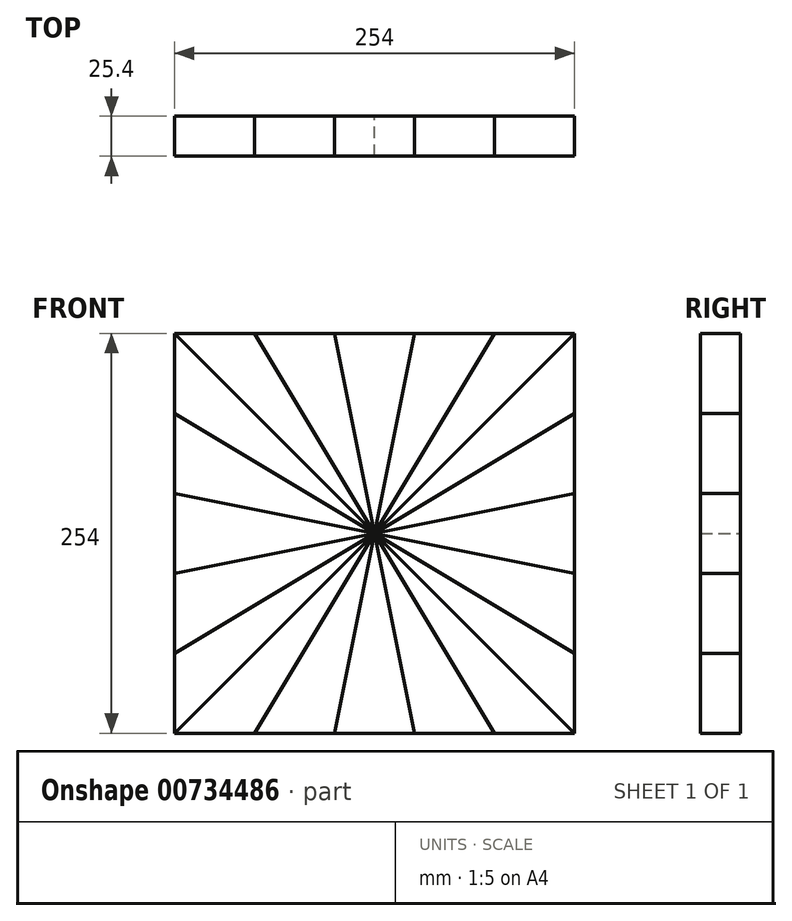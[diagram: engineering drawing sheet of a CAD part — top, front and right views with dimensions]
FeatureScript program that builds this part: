
annotation { "Feature Type Name" : "Feature", "Feature Type Description" : "" }
export const myFeature = defineFeature(function(context is Context, id is Id, definition is map)
    precondition{}
    {
        {
            var Q0;
            Q0=qCreatedBy(makeId("Front.planeOp"),FACE);
            var sketch = newSketch(context, id + "F0", { "sketchPlane" : qUnion([Q0])});
            skLineSegment(sketch, "E0.top", {"start": v(0, 127) * mm, "end": v(-127, 127) * mm});
            skLineSegment(sketch, "E1", {"start": v(0, 0) * mm, "end": v(-25.4, 127) * mm});
            skLineSegment(sketch, "E2", {"start": v(0, 0) * mm, "end": v(-127, 127) * mm});
            skPoint(sketch, "E3.end.orphan", {"position": v(-63.5, 127) * mm});
            skLineSegment(sketch, "E4", {"start": v(0, 0) * mm, "end": v(-76.2, 127) * mm});
            skLineSegment(sketch, "E5.MirrorCS", {"start": v(-127, 0) * mm, "end": v(-127, 127) * mm});
            skPoint(sketch, "E6.MirrorP", {"position": v(-127, 63.5) * mm});
            skLineSegment(sketch, "E7.MirrorCS", {"start": v(0, 0) * mm, "end": v(-127, 76.2) * mm});
            skLineSegment(sketch, "E8.MirrorCS", {"start": v(0, 0) * mm, "end": v(-127, 25.4) * mm});
            skLineSegment(sketch, "E9.MirrorCS", {"start": v(0, 0) * mm, "end": v(127, 25.4) * mm});
            skLineSegment(sketch, "E10.MirrorCS", {"start": v(0, 0) * mm, "end": v(127, 76.2) * mm});
            skPoint(sketch, "E11.MirrorP", {"position": v(63.5, 127) * mm});
            skPoint(sketch, "E12.MirrorP", {"position": v(127, 63.5) * mm});
            skLineSegment(sketch, "E13.MirrorCS", {"start": v(0, 0) * mm, "end": v(25.4, 127) * mm});
            skLineSegment(sketch, "E14.MirrorCS", {"start": v(0, 127) * mm, "end": v(127, 127) * mm});
            skLineSegment(sketch, "E15.MirrorCS", {"start": v(0, 0) * mm, "end": v(127, 127) * mm});
            skLineSegment(sketch, "E16.MirrorCS", {"start": v(127, 0) * mm, "end": v(127, 127) * mm});
            skLineSegment(sketch, "E17.MirrorCS", {"start": v(0, 0) * mm, "end": v(76.2, 127) * mm});
            skLineSegment(sketch, "E18.MirrorCS", {"start": v(0, -127) * mm, "end": v(127, -127) * mm});
            skLineSegment(sketch, "E19.MirrorCS", {"start": v(127, 0) * mm, "end": v(127, -127) * mm});
            skLineSegment(sketch, "E20.MirrorCS", {"start": v(0, 0) * mm, "end": v(-76.2, -127) * mm});
            skLineSegment(sketch, "E21.MirrorCS", {"start": v(0, 0) * mm, "end": v(-127, -25.4) * mm});
            skLineSegment(sketch, "E22.MirrorCS", {"start": v(0, 0) * mm, "end": v(76.2, -127) * mm});
            skPoint(sketch, "E23.MirrorP", {"position": v(127, -63.5) * mm});
            skLineSegment(sketch, "E24.MirrorCS", {"start": v(0, 0) * mm, "end": v(127, -25.4) * mm});
            skLineSegment(sketch, "E25.MirrorCS", {"start": v(0, 0) * mm, "end": v(-25.4, -127) * mm});
            skLineSegment(sketch, "E26.MirrorCS", {"start": v(0, 0) * mm, "end": v(127, -76.2) * mm});
            skLineSegment(sketch, "E27.MirrorCS", {"start": v(-127, 0) * mm, "end": v(-127, -127) * mm});
            skLineSegment(sketch, "E28.MirrorCS", {"start": v(0, 0) * mm, "end": v(25.4, -127) * mm});
            skPoint(sketch, "E29.MirrorP", {"position": v(63.5, -127) * mm});
            skLineSegment(sketch, "E30.MirrorCS", {"start": v(0, 0) * mm, "end": v(127, -127) * mm});
            skPoint(sketch, "E31.MirrorP", {"position": v(-63.5, -127) * mm});
            skLineSegment(sketch, "E32.MirrorCS", {"start": v(0, 0) * mm, "end": v(-127, -76.2) * mm});
            skPoint(sketch, "E33.MirrorP", {"position": v(-127, -63.5) * mm});
            skLineSegment(sketch, "E34.MirrorCS", {"start": v(0, 0) * mm, "end": v(-127, -127) * mm});
            skLineSegment(sketch, "E35.MirrorCS", {"start": v(0, -127) * mm, "end": v(-127, -127) * mm});
            skSolve(sketch);
        }
        {
            var Q0;
            {var subQ0=sQuery(id+"F0.wireOp",EDGE,"E2");Q0=makeQuery(id+"F0.imprint","IMPRINT",FACE,{"disambiguationData":[TD([[makeQuery(id+"F0.imprint","IMPRINT",EDGE,{"derivedFrom":subQ0}),1.0]])]});}
            extrude(context, id + "F1", {"entities" : qUnion([Q0]), "depth" : 25.4 * mm, "offsetDistance" : 25.4 * mm});
        }
        {
            var Q0;
            {var subQ0=sQuery(id+"F0.wireOp",EDGE,"E2");Q0=makeQuery(id+"F0.imprint","IMPRINT",FACE,{"disambiguationData":[TD([[makeQuery(id+"F0.imprint","IMPRINT",EDGE,{"derivedFrom":subQ0}),-1.0]])]});}
            extrude(context, id + "F2", {"entities" : qUnion([Q0]), "depth" : 25.4 * mm, "offsetDistance" : 25.4 * mm});
        }
        {
            var Q0;
            {var subQ0=sQuery(id+"F0.wireOp",EDGE,"E1");Q0=makeQuery(id+"F0.imprint","IMPRINT",FACE,{"disambiguationData":[TD([[makeQuery(id+"F0.imprint","IMPRINT",EDGE,{"derivedFrom":subQ0}),1.0]])]});}
            var Q1;
            {var subQ4=sQuery(id+"F0.wireOp",EDGE,"E25.MirrorCS");Q1=makeQuery(id+"F0.imprint","IMPRINT",FACE,{"disambiguationData":[TD([[makeQuery(id+"F0.imprint","IMPRINT",EDGE,{"derivedFrom":subQ4}),1.0]])]});}
            extrude(context, id + "F3", {"entities" : qUnion([Q0, Q1]), "depth" : 25.4 * mm, "offsetDistance" : 25.4 * mm});
        }
        {
            var Q0;
            {var subQ3=sQuery(id+"F0.wireOp",EDGE,"E1");Q0=makeQuery(id+"F0.imprint","IMPRINT",FACE,{"disambiguationData":[TD([[makeQuery(id+"F0.imprint","IMPRINT",EDGE,{"derivedFrom":subQ3}),-1.0]])]});}
            var Q1;
            {var subQ0=sQuery(id+"F0.wireOp",EDGE,"E20.MirrorCS");Q1=makeQuery(id+"F0.imprint","IMPRINT",FACE,{"disambiguationData":[TD([[makeQuery(id+"F0.imprint","IMPRINT",EDGE,{"derivedFrom":subQ0}),1.0]])]});}
            extrude(context, id + "F4", {"entities" : qUnion([Q0, Q1]), "depth" : 25.4 * mm, "offsetDistance" : 25.4 * mm});
        }
        {
            var Q0;
            {var subQ0=sQuery(id+"F0.wireOp",EDGE,"E13.MirrorCS");Q0=makeQuery(id+"F0.imprint","IMPRINT",FACE,{"disambiguationData":[TD([[makeQuery(id+"F0.imprint","IMPRINT",EDGE,{"derivedFrom":subQ0}),-1.0]])]});}
            var Q1;
            {var subQ0=sQuery(id+"F0.wireOp",EDGE,"E20.MirrorCS");Q1=makeQuery(id+"F0.imprint","IMPRINT",FACE,{"disambiguationData":[TD([[makeQuery(id+"F0.imprint","IMPRINT",EDGE,{"derivedFrom":subQ0}),-1.0]])]});}
            extrude(context, id + "F5", {"entities" : qUnion([Q0, Q1]), "depth" : 25.4 * mm, "offsetDistance" : 25.4 * mm});
        }
        {
            var Q0;
            {var subQ2=sQuery(id+"F0.wireOp",EDGE,"E32.MirrorCS");Q0=makeQuery(id+"F0.imprint","IMPRINT",FACE,{"disambiguationData":[TD([[makeQuery(id+"F0.imprint","IMPRINT",EDGE,{"derivedFrom":subQ2}),1.0]])]});}
            extrude(context, id + "F6", {"entities" : qUnion([Q0]), "depth" : 25.4 * mm, "offsetDistance" : 25.4 * mm});
        }
        {
            var Q0;
            {var subQ0=sQuery(id+"F0.wireOp",EDGE,"E15.MirrorCS");Q0=makeQuery(id+"F0.imprint","IMPRINT",FACE,{"disambiguationData":[TD([[makeQuery(id+"F0.imprint","IMPRINT",EDGE,{"derivedFrom":subQ0}),1.0]])]});}
            var Q1;
            {var subQ0=sQuery(id+"F0.wireOp",EDGE,"E21.MirrorCS");Q1=makeQuery(id+"F0.imprint","IMPRINT",FACE,{"disambiguationData":[TD([[makeQuery(id+"F0.imprint","IMPRINT",EDGE,{"derivedFrom":subQ0}),1.0]])]});}
            extrude(context, id + "F7", {"entities" : qUnion([Q0, Q1]), "depth" : 25.4 * mm, "offsetDistance" : 25.4 * mm});
        }
        {
            var Q0;
            {var subQ0=sQuery(id+"F0.wireOp",EDGE,"E10.MirrorCS");Q0=makeQuery(id+"F0.imprint","IMPRINT",FACE,{"disambiguationData":[TD([[makeQuery(id+"F0.imprint","IMPRINT",EDGE,{"derivedFrom":subQ0}),1.0]])]});}
            var Q1;
            {var subQ0=sQuery(id+"F0.wireOp",EDGE,"E22.MirrorCS");Q1=makeQuery(id+"F0.imprint","IMPRINT",FACE,{"disambiguationData":[TD([[makeQuery(id+"F0.imprint","IMPRINT",EDGE,{"derivedFrom":subQ0}),-1.0]])]});}
            extrude(context, id + "F8", {"entities" : qUnion([Q0, Q1]), "depth" : 25.4 * mm, "offsetDistance" : 25.4 * mm});
        }
        {
            var Q0;
            {var subQ0=sQuery(id+"F0.wireOp",EDGE,"E9.MirrorCS");Q0=makeQuery(id+"F0.imprint","IMPRINT",FACE,{"disambiguationData":[TD([[makeQuery(id+"F0.imprint","IMPRINT",EDGE,{"derivedFrom":subQ0}),1.0]])]});}
            var Q1;
            {var subQ2=sQuery(id+"F0.wireOp",EDGE,"E22.MirrorCS");Q1=makeQuery(id+"F0.imprint","IMPRINT",FACE,{"disambiguationData":[TD([[makeQuery(id+"F0.imprint","IMPRINT",EDGE,{"derivedFrom":subQ2}),1.0]])]});}
            extrude(context, id + "F9", {"entities" : qUnion([Q0, Q1]), "depth" : 25.4 * mm, "offsetDistance" : 25.4 * mm});
        }
        {
            var Q0;
            {var subQ0=sQuery(id+"F0.wireOp",EDGE,"E9.MirrorCS");Q0=makeQuery(id+"F0.imprint","IMPRINT",FACE,{"disambiguationData":[TD([[makeQuery(id+"F0.imprint","IMPRINT",EDGE,{"derivedFrom":subQ0}),-1.0]])]});}
            var Q1;
            {var subQ3=sQuery(id+"F0.wireOp",EDGE,"E8.MirrorCS");Q1=makeQuery(id+"F0.imprint","IMPRINT",FACE,{"disambiguationData":[TD([[makeQuery(id+"F0.imprint","IMPRINT",EDGE,{"derivedFrom":subQ3}),1.0]])]});}
            extrude(context, id + "F10", {"entities" : qUnion([Q0, Q1]), "depth" : 25.4 * mm, "offsetDistance" : 25.4 * mm});
        }
        {
            var Q0;
            {var subQ2=sQuery(id+"F0.wireOp",EDGE,"E26.MirrorCS");Q0=makeQuery(id+"F0.imprint","IMPRINT",FACE,{"disambiguationData":[TD([[makeQuery(id+"F0.imprint","IMPRINT",EDGE,{"derivedFrom":subQ2}),-1.0]])]});}
            var Q1;
            {var subQ0=sQuery(id+"F0.wireOp",EDGE,"E7.MirrorCS");Q1=makeQuery(id+"F0.imprint","IMPRINT",FACE,{"disambiguationData":[TD([[makeQuery(id+"F0.imprint","IMPRINT",EDGE,{"derivedFrom":subQ0}),1.0]])]});}
            extrude(context, id + "F11", {"entities" : qUnion([Q0, Q1]), "depth" : 25.4 * mm, "offsetDistance" : 25.4 * mm});
        }
        {
            var Q0;
            {var subQ0=sQuery(id+"F0.wireOp",EDGE,"E24.MirrorCS");Q0=makeQuery(id+"F0.imprint","IMPRINT",FACE,{"disambiguationData":[TD([[makeQuery(id+"F0.imprint","IMPRINT",EDGE,{"derivedFrom":subQ0}),-1.0]])]});}
            extrude(context, id + "F12", {"entities" : qUnion([Q0]), "depth" : 25.4 * mm, "offsetDistance" : 25.4 * mm});
        }
    });
